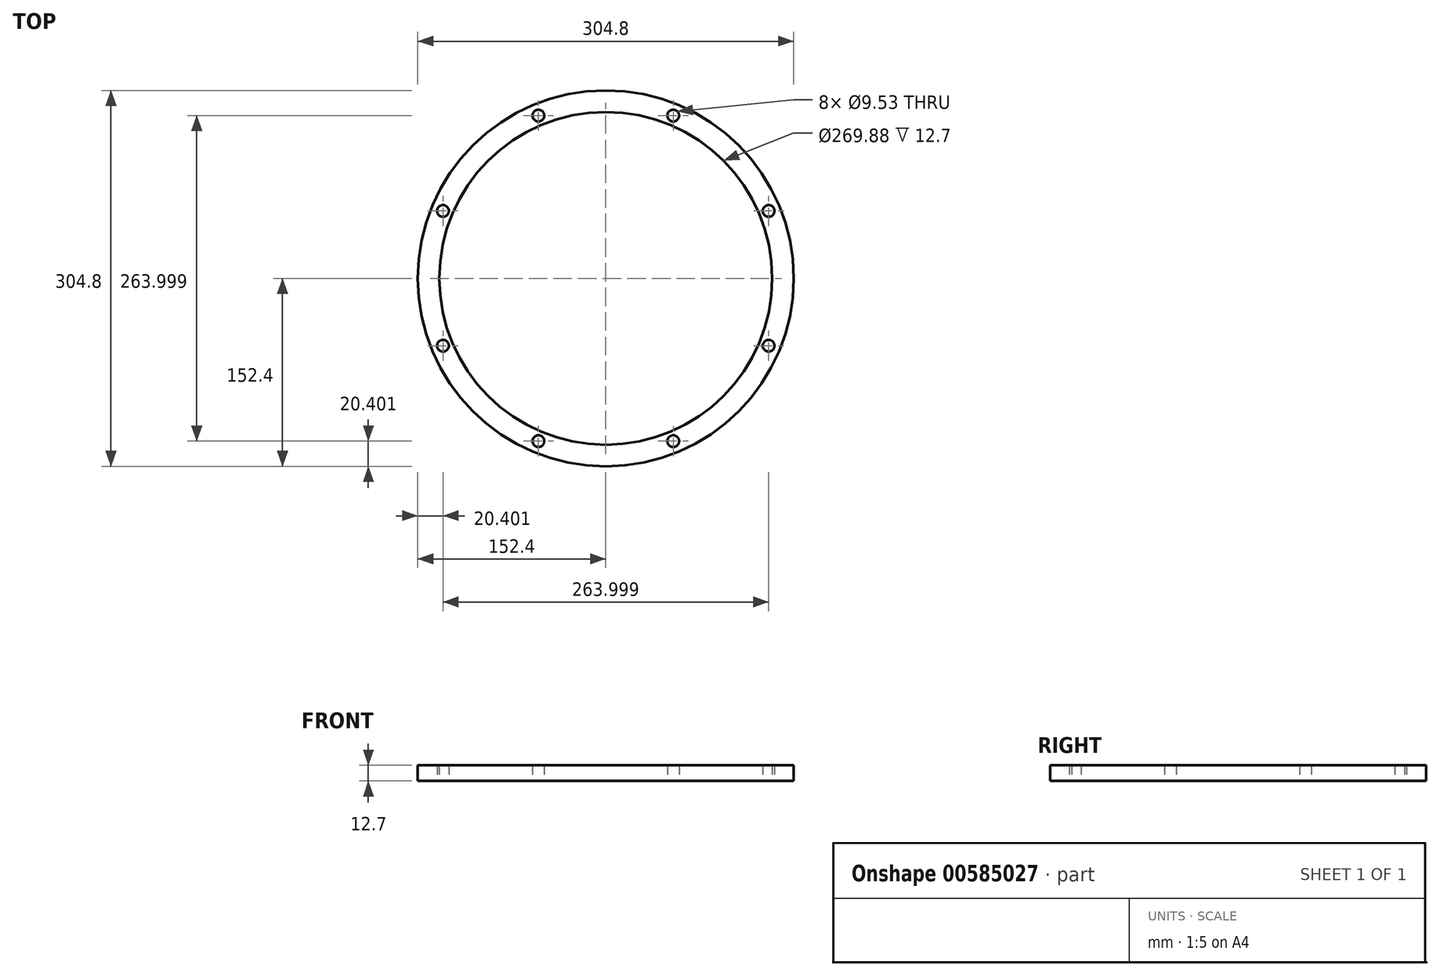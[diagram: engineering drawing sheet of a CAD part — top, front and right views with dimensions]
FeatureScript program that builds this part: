
annotation { "Feature Type Name" : "Feature", "Feature Type Description" : "" }
export const myFeature = defineFeature(function(context is Context, id is Id, definition is map)
    precondition{}
    {
        {
            var Q0;
            Q0=qCreatedBy(makeId("Top.planeOp"),FACE);
            var sketch = newSketch(context, id + "F0", { "sketchPlane" : qUnion([Q0])});
            skCircle(sketch, "E0", {"center": v(0, 0) * mm, "radius": 134.94 * mm});
            skCircle(sketch, "E1", {"center": v(0, 0) * mm, "radius": 152.4 * mm});
            skCircle(sketch, "E2", {"center": v(0, 0) * mm, "radius": 142.88 * mm, "construction": true});
            skCircle(sketch, "E3", {"center": v(54.68, 132) * mm, "radius": 4.76 * mm});
            skCircle(sketch, "E4.1.0", {"center": v(-54.68, 132) * mm, "radius": 4.76 * mm});
            skCircle(sketch, "E4.2.0", {"center": v(-132, 54.68) * mm, "radius": 4.76 * mm});
            skCircle(sketch, "E4.3.0", {"center": v(-132, -54.68) * mm, "radius": 4.76 * mm});
            skCircle(sketch, "E4.4.0", {"center": v(-54.68, -132) * mm, "radius": 4.76 * mm});
            skCircle(sketch, "E4.5.0", {"center": v(54.68, -132) * mm, "radius": 4.76 * mm});
            skCircle(sketch, "E4.6.0", {"center": v(132, -54.68) * mm, "radius": 4.76 * mm});
            skCircle(sketch, "E4.7.0", {"center": v(132, 54.68) * mm, "radius": 4.76 * mm});
            skSolve(sketch);
        }
        {
            var Q0;
            Q0 = qSketchRegion(id + "F0", true);
            extrude(context, id + "F1", {"entities" : qUnion([Q0]), "depth" : 12.7 * mm, "offsetDistance" : 25.4 * mm});
        }
    });
